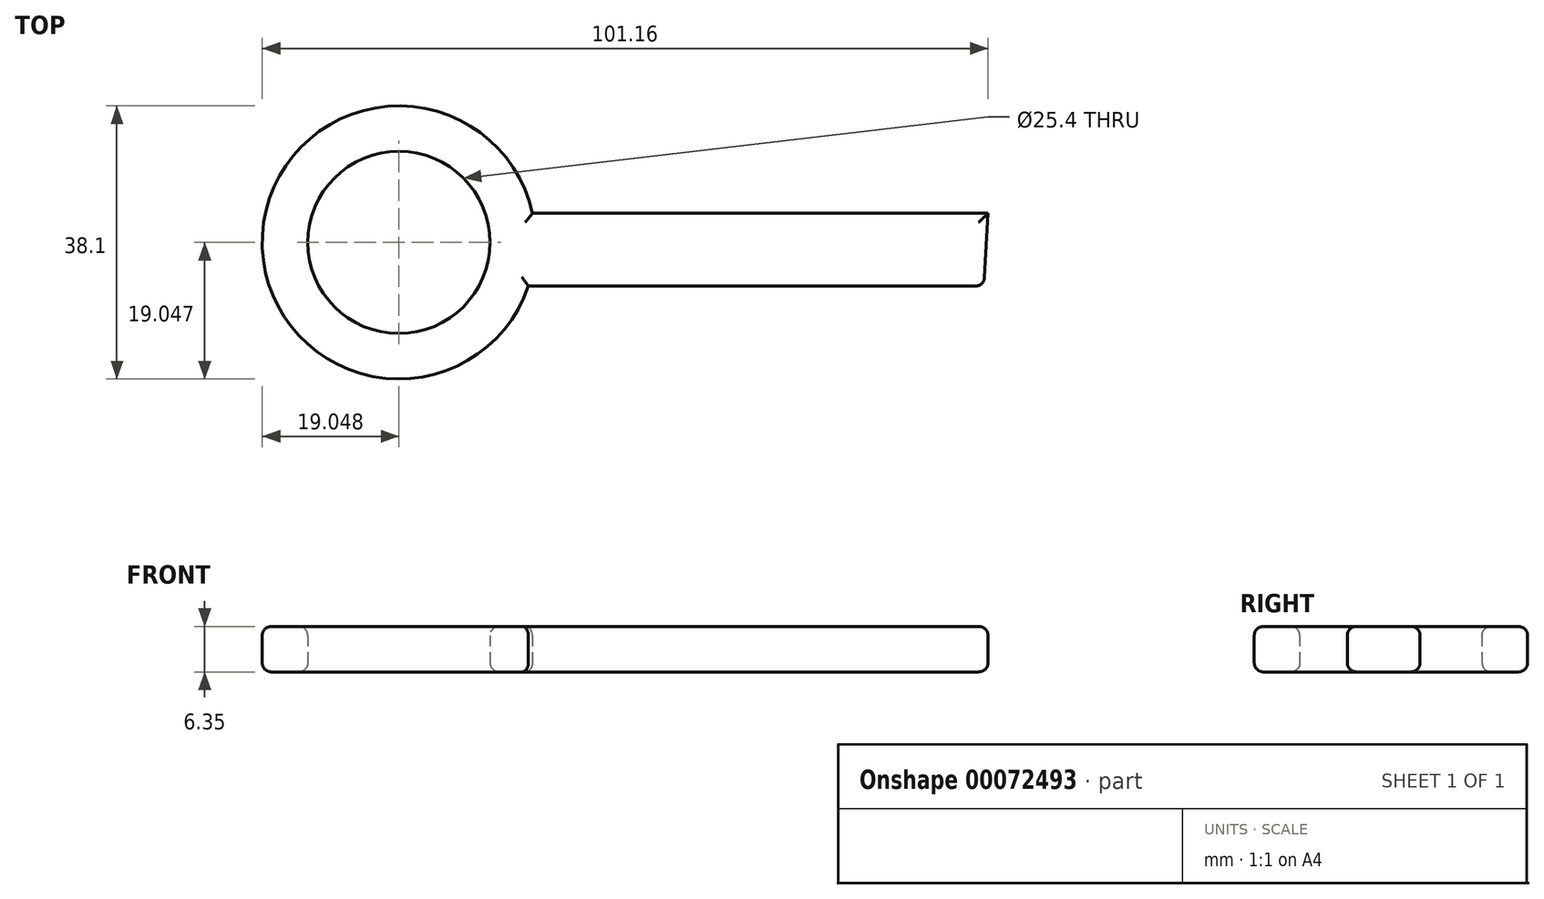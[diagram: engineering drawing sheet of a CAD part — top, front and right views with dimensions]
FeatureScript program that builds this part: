
annotation { "Feature Type Name" : "Feature", "Feature Type Description" : "" }
export const myFeature = defineFeature(function(context is Context, id is Id, definition is map)
    precondition{}
    {
        {
            var Q0;
            Q0=qCreatedBy(makeId("Top.planeOp"),FACE);
            var sketch = newSketch(context, id + "F0", { "sketchPlane" : qUnion([Q0])});
            skCircle(sketch, "E0", {"center": v(-43.78, 37.78) * mm, "radius": 19.05 * mm});
            skCircle(sketch, "E1", {"center": v(-43.78, 37.78) * mm, "radius": 12.7 * mm});
            skLineSegment(sketch, "E2", {"start": v(-25.17, 41.83) * mm, "end": v(38.33, 41.83) * mm});
            skLineSegment(sketch, "E3", {"start": v(-25.73, 31.69) * mm, "end": v(37.77, 31.69) * mm});
            skLineSegment(sketch, "E4", {"start": v(37.77, 31.69) * mm, "end": v(38.33, 41.83) * mm});
            skLineSegment(sketch, "E5.bottom", {"start": v(26.9, 31.69) * mm, "end": v(20.55, 31.69) * mm});
            skLineSegment(sketch, "E5.top", {"start": v(26.9, 15.18) * mm, "end": v(20.55, 15.18) * mm});
            skLineSegment(sketch, "E5.left", {"start": v(26.9, 31.69) * mm, "end": v(26.9, 15.18) * mm});
            skLineSegment(sketch, "E5.right", {"start": v(20.55, 31.69) * mm, "end": v(20.55, 15.18) * mm});
            skPoint(sketch, "E6.oppositeSnap0", {"position": v(6.02, 31.69) * mm});
            skLineSegment(sketch, "E6.bottom", {"start": v(12.37, 31.69) * mm, "end": v(6.02, 31.69) * mm});
            skLineSegment(sketch, "E6.top", {"start": v(12.37, 15.18) * mm, "end": v(6.02, 15.18) * mm});
            skLineSegment(sketch, "E6.left", {"start": v(12.37, 31.69) * mm, "end": v(12.37, 15.18) * mm});
            skLineSegment(sketch, "E6.right", {"start": v(6.02, 31.69) * mm, "end": v(6.02, 15.18) * mm});
            skSolve(sketch);
        }
        {
            var Q0;
            Q0=makeQuery(id+"F0.imprint","IMPRINT",FACE,{"disambiguationData":[TD([[makeQuery(id+"F0.imprint","IMPRINT",EDGE,{"derivedFrom":sQuery(id+"F0.wireOp",EDGE,"E6.bottom")}),1.0]])]});
            var Q1;
            Q1=makeQuery(id+"F0.imprint","IMPRINT",FACE,{"disambiguationData":[TD([[makeQuery(id+"F0.imprint","IMPRINT",EDGE,{"derivedFrom":sQuery(id+"F0.wireOp",EDGE,"E5.bottom")}),1.0]])]});
            var Q2;
            {var subQ5=sQuery(id+"F0.wireOp",EDGE,"E2");Q2=makeQuery(id+"F0.imprint","IMPRINT",FACE,{"disambiguationData":[TD([[makeQuery(id+"F0.imprint","IMPRINT",EDGE,{"derivedFrom":subQ5}),-1.0]])]});}
            var Q3;
            Q3=makeQuery(id+"F0.imprint","IMPRINT",FACE,{"disambiguationData":[TD([[makeQuery(id+"F0.imprint","IMPRINT",EDGE,{"derivedFrom":sQuery(id+"F0.wireOp",EDGE,"E1")}),-1.0]])]});
            extrude(context, id + "F1", {"entities" : qUnion([Q0, Q1, Q2, Q3]), "depth" : 6.35 * mm});
        }
        {
            var Q0;
            Q0=makeQuery(id+"F1.opExtrude","CAP_EDGE",EDGE,{"disambiguationData":[OSD([sQuery(id+"F0.wireOp",EDGE,"E4")])],"isStart":false});
            var Q1;
            Q1=makeQuery(id+"F1.opExtrude","CAP_EDGE",EDGE,{"disambiguationData":[OSD([sQuery(id+"F0.wireOp",EDGE,"E2")])],"isStart":false});
            var Q2;
            Q2=makeQuery(id+"F1.opExtrude","CAP_EDGE",EDGE,{"disambiguationData":[OSD([sQuery(id+"F0.wireOp",EDGE,"E5.left")])],"isStart":false});
            var Q3;
            Q3=makeQuery(id+"F1.opExtrude","CAP_EDGE",EDGE,{"disambiguationData":[OSD([sQuery(id+"F0.wireOp",EDGE,"E5.right")])],"isStart":false});
            var Q4;
            Q4=makeQuery(id+"F1.opExtrude","CAP_EDGE",EDGE,{"disambiguationData":[OSD([sQuery(id+"F0.wireOp",EDGE,"E5.top")])],"isStart":true});
            var Q5;
            {var subQ0=sQuery(id+"F0.wireOp",EDGE,"E3");Q5=makeQuery(id+"F1.opExtrude","CAP_EDGE",EDGE,{"disambiguationData":[OSD([subQ0]),TDD([makeQuery(id+"F0.imprint","IMPRINT",EDGE,{"disambiguationData":[TD([[makeQuery(id+"F0.imprint","INTERSECT",VERTEX,{"derivedFrom":[subQ0,sQuery(id+"F0.wireOp",EDGE,"E5.bottom"),sQuery(id+"F0.wireOp",EDGE,"E5.right")]}),1.0]])],"derivedFrom":subQ0})])],"isStart":false});}
            var Q6;
            Q6=makeQuery(id+"F1.opExtrude","CAP_EDGE",EDGE,{"disambiguationData":[OSD([sQuery(id+"F0.wireOp",EDGE,"E6.left")])],"isStart":false});
            var Q7;
            Q7=makeQuery(id+"F1.opExtrude","CAP_EDGE",EDGE,{"disambiguationData":[OSD([sQuery(id+"F0.wireOp",EDGE,"E6.top")])],"isStart":false});
            var Q8;
            Q8=makeQuery(id+"F1.opExtrude","CAP_FACE",FACE,{"disambiguationData":[OSD([sQuery(id+"F0.wireOp",EDGE,"E0"),sQuery(id+"F0.wireOp",EDGE,"E1"),sQuery(id+"F0.wireOp",EDGE,"E2"),sQuery(id+"F0.wireOp",EDGE,"E3"),sQuery(id+"F0.wireOp",EDGE,"E4"),sQuery(id+"F0.wireOp",EDGE,"E5.top"),sQuery(id+"F0.wireOp",EDGE,"E5.left"),sQuery(id+"F0.wireOp",EDGE,"E5.right"),sQuery(id+"F0.wireOp",EDGE,"E6.top"),sQuery(id+"F0.wireOp",EDGE,"E6.left"),sQuery(id+"F0.wireOp",EDGE,"E6.right")])],"isStart":false});
            var Q9;
            {var subQ0=sQuery(id+"F0.wireOp",EDGE,"E3");Q9=makeQuery(id+"F1.opExtrude","CAP_EDGE",EDGE,{"disambiguationData":[OSD([subQ0]),TDD([makeQuery(id+"F0.imprint","IMPRINT",EDGE,{"disambiguationData":[TD([[makeQuery(id+"F0.imprint","INTERSECT",VERTEX,{"derivedFrom":[subQ0,sQuery(id+"F0.wireOp",EDGE,"E4")]}),1.0]])],"derivedFrom":subQ0})])],"isStart":true});}
            var Q10;
            Q10=makeQuery(id+"F1.opExtrude","CAP_EDGE",EDGE,{"disambiguationData":[OSD([sQuery(id+"F0.wireOp",EDGE,"E6.top")])],"isStart":true});
            fillet(context, id + "F2", {"entities" : qUnion([Q0, Q1, Q2, Q3, Q4, Q5, Q6, Q7, Q8, Q9, Q10]), "radius" : 1.27 * mm, "tangentPropagation" : true, "allowEdgeOverflow" : false});
        }
        {
            var Q0;
            Q0=makeQuery(id+"F1.opExtrude","CAP_EDGE",EDGE,{"disambiguationData":[OSD([sQuery(id+"F0.wireOp",EDGE,"E1")])],"isStart":true});
            var Q1;
            Q1=makeQuery(id+"F1.opExtrude","CAP_EDGE",EDGE,{"disambiguationData":[OSD([sQuery(id+"F0.wireOp",EDGE,"E0")])],"isStart":true});
            var Q2;
            Q2=makeQuery(id+"F1.opExtrude","CAP_EDGE",EDGE,{"disambiguationData":[OSD([sQuery(id+"F0.wireOp",EDGE,"E2")])],"isStart":true});
            var Q3;
            {var subQ0=sQuery(id+"F0.wireOp",EDGE,"E6.top");Q3=makeQuery(id+"F2.opFillet","BLEND_EDGE",EDGE,{"blendedFrom":[makeQuery(id+"F1.opExtrude","CAP_EDGE",EDGE,{"disambiguationData":[OSD([subQ0])],"isStart":true}),makeQuery(id+"F1.opExtrude","CAP_FACE",FACE,{"disambiguationData":[OSD([sQuery(id+"F0.wireOp",EDGE,"E0"),sQuery(id+"F0.wireOp",EDGE,"E1"),sQuery(id+"F0.wireOp",EDGE,"E2"),sQuery(id+"F0.wireOp",EDGE,"E3"),sQuery(id+"F0.wireOp",EDGE,"E4"),sQuery(id+"F0.wireOp",EDGE,"E5.top"),sQuery(id+"F0.wireOp",EDGE,"E5.left"),sQuery(id+"F0.wireOp",EDGE,"E5.right"),subQ0,sQuery(id+"F0.wireOp",EDGE,"E6.left"),sQuery(id+"F0.wireOp",EDGE,"E6.right")])],"isStart":true})],"blendedInto":[makeQuery(id+"F1.opExtrude","CAP_FACE",FACE,{"disambiguationData":[OSD([sQuery(id+"F0.wireOp",EDGE,"E0"),sQuery(id+"F0.wireOp",EDGE,"E1"),sQuery(id+"F0.wireOp",EDGE,"E2"),sQuery(id+"F0.wireOp",EDGE,"E3"),sQuery(id+"F0.wireOp",EDGE,"E4"),sQuery(id+"F0.wireOp",EDGE,"E5.top"),sQuery(id+"F0.wireOp",EDGE,"E5.left"),sQuery(id+"F0.wireOp",EDGE,"E5.right"),subQ0,sQuery(id+"F0.wireOp",EDGE,"E6.left"),sQuery(id+"F0.wireOp",EDGE,"E6.right")])],"isStart":true})]});}
            var Q4;
            Q4=makeQuery(id+"F1.opExtrude","CAP_EDGE",EDGE,{"disambiguationData":[OSD([sQuery(id+"F0.wireOp",EDGE,"E6.left")])],"isStart":true});
            var Q5;
            {var subQ0=sQuery(id+"F0.wireOp",EDGE,"E3");Q5=makeQuery(id+"F1.opExtrude","CAP_EDGE",EDGE,{"disambiguationData":[OSD([subQ0]),TDD([makeQuery(id+"F0.imprint","IMPRINT",EDGE,{"disambiguationData":[TD([[makeQuery(id+"F0.imprint","INTERSECT",VERTEX,{"derivedFrom":[subQ0,sQuery(id+"F0.wireOp",EDGE,"E5.bottom"),sQuery(id+"F0.wireOp",EDGE,"E5.right")]}),1.0]])],"derivedFrom":subQ0})])],"isStart":true});}
            var Q6;
            {var subQ0=sQuery(id+"F0.wireOp",EDGE,"E5.top");Q6=makeQuery(id+"F2.opFillet","BLEND_EDGE",EDGE,{"blendedFrom":[makeQuery(id+"F1.opExtrude","CAP_EDGE",EDGE,{"disambiguationData":[OSD([subQ0])],"isStart":true}),makeQuery(id+"F1.opExtrude","CAP_FACE",FACE,{"disambiguationData":[OSD([sQuery(id+"F0.wireOp",EDGE,"E0"),sQuery(id+"F0.wireOp",EDGE,"E1"),sQuery(id+"F0.wireOp",EDGE,"E2"),sQuery(id+"F0.wireOp",EDGE,"E3"),sQuery(id+"F0.wireOp",EDGE,"E4"),subQ0,sQuery(id+"F0.wireOp",EDGE,"E5.left"),sQuery(id+"F0.wireOp",EDGE,"E5.right"),sQuery(id+"F0.wireOp",EDGE,"E6.top"),sQuery(id+"F0.wireOp",EDGE,"E6.left"),sQuery(id+"F0.wireOp",EDGE,"E6.right")])],"isStart":true})],"blendedInto":[makeQuery(id+"F1.opExtrude","CAP_FACE",FACE,{"disambiguationData":[OSD([sQuery(id+"F0.wireOp",EDGE,"E0"),sQuery(id+"F0.wireOp",EDGE,"E1"),sQuery(id+"F0.wireOp",EDGE,"E2"),sQuery(id+"F0.wireOp",EDGE,"E3"),sQuery(id+"F0.wireOp",EDGE,"E4"),subQ0,sQuery(id+"F0.wireOp",EDGE,"E5.left"),sQuery(id+"F0.wireOp",EDGE,"E5.right"),sQuery(id+"F0.wireOp",EDGE,"E6.top"),sQuery(id+"F0.wireOp",EDGE,"E6.left"),sQuery(id+"F0.wireOp",EDGE,"E6.right")])],"isStart":true})]});}
            var Q7;
            Q7=makeQuery(id+"F1.opExtrude","CAP_EDGE",EDGE,{"disambiguationData":[OSD([sQuery(id+"F0.wireOp",EDGE,"E5.right")])],"isStart":true});
            var Q8;
            Q8=makeQuery(id+"F1.opExtrude","CAP_EDGE",EDGE,{"disambiguationData":[OSD([sQuery(id+"F0.wireOp",EDGE,"E5.left")])],"isStart":true});
            var Q9;
            {var subQ0=sQuery(id+"F0.wireOp",EDGE,"E5.left");var subQ1=sQuery(id+"F0.wireOp",EDGE,"E4");var subQ2=sQuery(id+"F0.wireOp",EDGE,"E3");Q9=makeQuery(id+"F2.opFillet","BLEND_EDGE",EDGE,{"blendedFrom":[makeQuery(id+"F1.opExtrude","CAP_EDGE",EDGE,{"disambiguationData":[OSD([subQ2]),TDD([makeQuery(id+"F0.imprint","IMPRINT",EDGE,{"disambiguationData":[TD([[makeQuery(id+"F0.imprint","INTERSECT",VERTEX,{"derivedFrom":[subQ2,subQ1]}),1.0]])],"derivedFrom":subQ2})])],"isStart":true}),makeQuery(id+"F1.opExtrude","CAP_FACE",FACE,{"disambiguationData":[OSD([sQuery(id+"F0.wireOp",EDGE,"E0"),sQuery(id+"F0.wireOp",EDGE,"E1"),sQuery(id+"F0.wireOp",EDGE,"E2"),subQ2,subQ1,sQuery(id+"F0.wireOp",EDGE,"E5.top"),subQ0,sQuery(id+"F0.wireOp",EDGE,"E5.right"),sQuery(id+"F0.wireOp",EDGE,"E6.top"),sQuery(id+"F0.wireOp",EDGE,"E6.left"),sQuery(id+"F0.wireOp",EDGE,"E6.right")])],"isStart":true})],"blendedInto":[makeQuery(id+"F1.opExtrude","CAP_FACE",FACE,{"disambiguationData":[OSD([sQuery(id+"F0.wireOp",EDGE,"E0"),sQuery(id+"F0.wireOp",EDGE,"E1"),sQuery(id+"F0.wireOp",EDGE,"E2"),subQ2,subQ1,sQuery(id+"F0.wireOp",EDGE,"E5.top"),subQ0,sQuery(id+"F0.wireOp",EDGE,"E5.right"),sQuery(id+"F0.wireOp",EDGE,"E6.top"),sQuery(id+"F0.wireOp",EDGE,"E6.left"),sQuery(id+"F0.wireOp",EDGE,"E6.right")])],"isStart":true})]});}
            var Q10;
            Q10=makeQuery(id+"F1.opExtrude","CAP_EDGE",EDGE,{"disambiguationData":[OSD([sQuery(id+"F0.wireOp",EDGE,"E4")])],"isStart":true});
            var Q11;
            {var subQ0=sQuery(id+"F0.wireOp",EDGE,"E3");Q11=makeQuery(id+"F1.opExtrude","CAP_EDGE",EDGE,{"disambiguationData":[OSD([subQ0]),TDD([makeQuery(id+"F0.imprint","IMPRINT",EDGE,{"disambiguationData":[TD([[makeQuery(id+"F0.imprint","INTERSECT",VERTEX,{"derivedFrom":[sQuery(id+"F0.wireOp",EDGE,"E0"),subQ0]}),-1.0]])],"derivedFrom":subQ0})])],"isStart":true});}
            fillet(context, id + "F3", {"entities" : qUnion([Q0, Q1, Q2, Q3, Q4, Q5, Q6, Q7, Q8, Q9, Q10, Q11]), "radius" : 1.27 * mm, "tangentPropagation" : true, "allowEdgeOverflow" : false});
        }
    });
